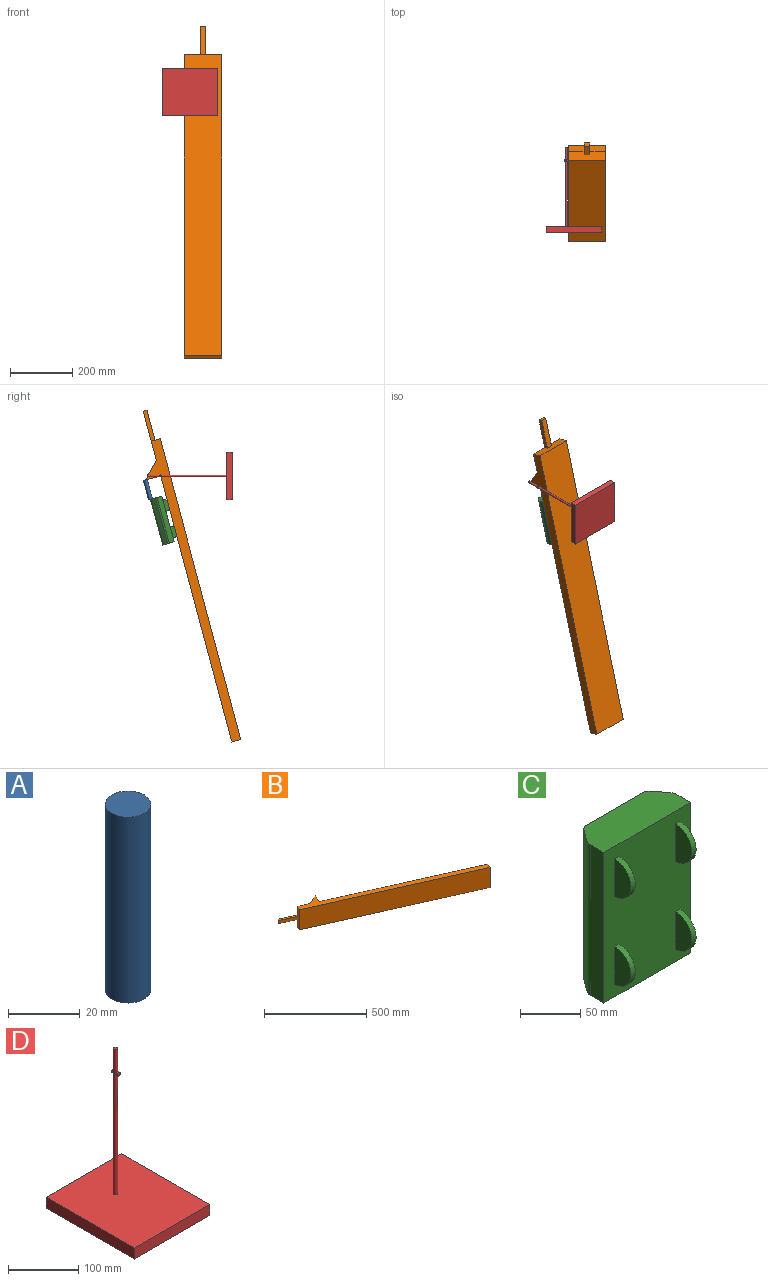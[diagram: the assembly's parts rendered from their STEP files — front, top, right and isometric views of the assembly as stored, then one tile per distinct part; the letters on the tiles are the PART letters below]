
ASSEMBLY  parts=4 mates=3
PART A: 3 faces, bbox 12.7x12.7x63.5 mm
  f0: cylinder r=6.35mm len=63.5mm, axis (0,0,-1), area 2533.5mm2, adj f1,f2
  f1: plane 12.7x12.7mm, normal (0,0,1), area 126.7mm2, adj f0
  f2: plane 12.7x12.7mm, normal (0,0,-1), area 126.7mm2, adj f0
PART B: 13 faces, bbox 1010.2x474.6x120 mm
  f0: plane 807.76x359.39mm, normal (0.41,0.91,0), area 106092mm2, adj f5,f7,f8,f11
  f1: plane 91.37x40.65mm, normal (-0.41,-0.91,0), area 1840mm2, adj f2,f3,f9,f10
  f2: plane 18.4x11.6mm, normal (-0.91,0.41,0), area 233.7mm2, adj f1,f6,f9,f10
  f3: plane 120x27.41mm, normal (-0.91,0.41,0), area 3366.3mm2, adj f1,f4,f6,f7,f8,f9,f10
  f4: plane 913.65x406.5mm, normal (-0.41,-0.91,0), area 120000mm2, adj f3,f5,f7,f8
  f5: plane 120x27.41mm, normal (0.91,-0.41,0), area 3600mm2, adj f0,f4,f7,f8
  f6: plane 150.84x120mm, normal (0.41,0.91,0), area 9652mm2, adj f2,f3,f7,f8,f9,f10,f12
  f7: plane 925.85x433.91mm, normal (0,0,1), area 31290.3mm2, adj f0,f3,f4,f5,f6,f11,f12
  f8: plane 925.85x433.91mm, normal (0,0,-1), area 31290.3mm2, adj f0,f3,f4,f5,f6,f11,f12
  f9: plane 96.53x52.25mm, normal (0,0,1), area 1270mm2, adj f1,f2,f3,f6
  f10: plane 96.53x52.25mm, normal (0,0,-1), area 1270mm2, adj f1,f2,f3,f6
  f11: plane 120x46.41mm, normal (0.91,-0.41,0), area 6096mm2, adj f0,f7,f8,f12
  f12: plane 120x67.06mm, normal (-0.36,0.93,0), area 8621mm2, adj f6,f7,f8,f11
PART C: 24 faces, bbox 101.6x57.2x152.4 mm
  f0: plane 152.4x101.6mm, normal (0,-1,0), area 14709.6mm2, adj f1,f5,f6,f7,f12,f13,f14,f15
  f1: plane 152.4x16.14mm, normal (1,0,0), area 2459.7mm2, adj f0,f6,f7,f10
  f2: plane 152.4x13.07mm, normal (0.81,0.59,0), area 2470.1mm2, adj f6,f7,f10,f11
  f3: plane 152.4x64.65mm, normal (0,1,0), area 9852.7mm2, adj f6,f7,f8,f11
  f4: plane 152.4x13.07mm, normal (-0.81,0.59,0), area 2470.1mm2, adj f6,f7,f8,f9
  f5: plane 152.4x16.14mm, normal (-1,0,0), area 2459.7mm2, adj f0,f6,f7,f9
  f6: plane 101.6x38.1mm, normal (0,0,1), area 3597.1mm2, adj f0,f1,f2,f3,f4,f5,f8,f9
  f7: plane 101.6x38.1mm, normal (0,0,-1), area 3597.1mm2, adj f0,f1,f2,f3,f4,f5,f8,f9
  f8: cylinder r=8.89mm len=152.4mm, axis (0,0,-1), area 1270.9mm2, adj f3,f4,f6,f7
  f9: cylinder r=8.89mm len=152.4mm, axis (0,0,-1), area 857.3mm2, adj f4,f5,f6,f7
  f10: cylinder r=8.89mm len=152.4mm, axis (0,0,-1), area 857.3mm2, adj f1,f2,f6,f7
  f11: cylinder r=8.89mm len=152.4mm, axis (0,0,-1), area 1270.9mm2, adj f2,f3,f6,f7
  f12: cylinder r=19.05mm len=38.1mm, axis (-1,0,0), area 304mm2, adj f0,f13,f14
  f13: plane 38.1x19.05mm, normal (-1,0,0), area 570mm2, adj f0,f12
  f14: plane 38.1x19.05mm, normal (1,0,0), area 570mm2, adj f0,f12
  f15: cylinder r=19.05mm len=38.1mm, axis (-1,0,0), area 304mm2, adj f0,f16,f17
  f16: plane 38.1x19.05mm, normal (-1,0,0), area 570mm2, adj f0,f15
  f17: plane 38.1x19.05mm, normal (1,0,0), area 570mm2, adj f0,f15
  f18: plane 38.1x19.05mm, normal (-1,0,0), area 570mm2, adj f0,f19
  f19: cylinder r=19.05mm len=38.1mm, axis (-1,0,0), area 304mm2, adj f0,f18,f20
  f20: plane 38.1x19.05mm, normal (1,0,0), area 570mm2, adj f0,f19
  f21: plane 38.1x19.05mm, normal (-1,0,0), area 570mm2, adj f0,f22
  f22: cylinder r=19.05mm len=38.1mm, axis (-1,0,0), area 304mm2, adj f0,f21,f23
  f23: plane 38.1x19.05mm, normal (1,0,0), area 570mm2, adj f0,f22
PART D: 11 faces, bbox 152.4x177.8x273.1 mm
  f0: cylinder r=3.17mm len=11.18mm, axis (0,1,0), area 143.1mm2, adj f1,f9,f10
  f1: cylinder r=3.17mm len=254mm, axis (0,0,-1), area 4987.2mm2, adj f0,f5,f8
  f2: plane 177.8x19.05mm, normal (-1,0,0), area 3387.1mm2, adj f3,f5,f6,f7
  f3: plane 177.8x152.4mm, normal (0,0,-1), area 27096.7mm2, adj f2,f4,f6,f7
  f4: plane 177.8x19.05mm, normal (1,0,0), area 3387.1mm2, adj f3,f5,f6,f7
  f5: plane 177.8x152.4mm, normal (0,0,1), area 27065.1mm2, adj f1,f2,f4,f6,f7
  f6: plane 152.4x19.05mm, normal (0,-1,0), area 2903.2mm2, adj f2,f3,f4,f5
  f7: plane 152.4x19.05mm, normal (0,1,0), area 2903.2mm2, adj f2,f3,f4,f5
  f8: plane 6.35x6.35mm, normal (0,0,1), area 31.7mm2, adj f1
  f9: plane 6.35x6.35mm, normal (0,-1,0), area 31.7mm2, adj f0
  f10: plane 6.35x6.35mm, normal (0,1,0), area 31.7mm2, adj f0
PLACE A rot(axis=(1,0,0),165deg) t=(-47.95,270.43,-13.53)mm
PLACE B rot(axis=(0.08,0.99,0.08),90.4deg) t=(-107.95,-105.43,-409.31)mm
PLACE C rot(axis=(-1,0,0),15deg) t=(-47.95,177.84,-212.25)mm
PLACE D rot(axis=(-0.58,0.58,0.58),120deg) t=(-177.8,-9.53,76.2)mm
MATE fastened C.f6 <-> A.f0  axis (0,0.26,0.97) through (-47.95,254.02,-74.87)mm
MATE fastened A.f0 <-> B.f11  axis (0,0.26,0.97) through (-47.95,270.43,-13.53)mm
MATE revolute D.f0 <-> B.f8  axis (1,0,0) through (-107.95,221.36,-0.4)mm
